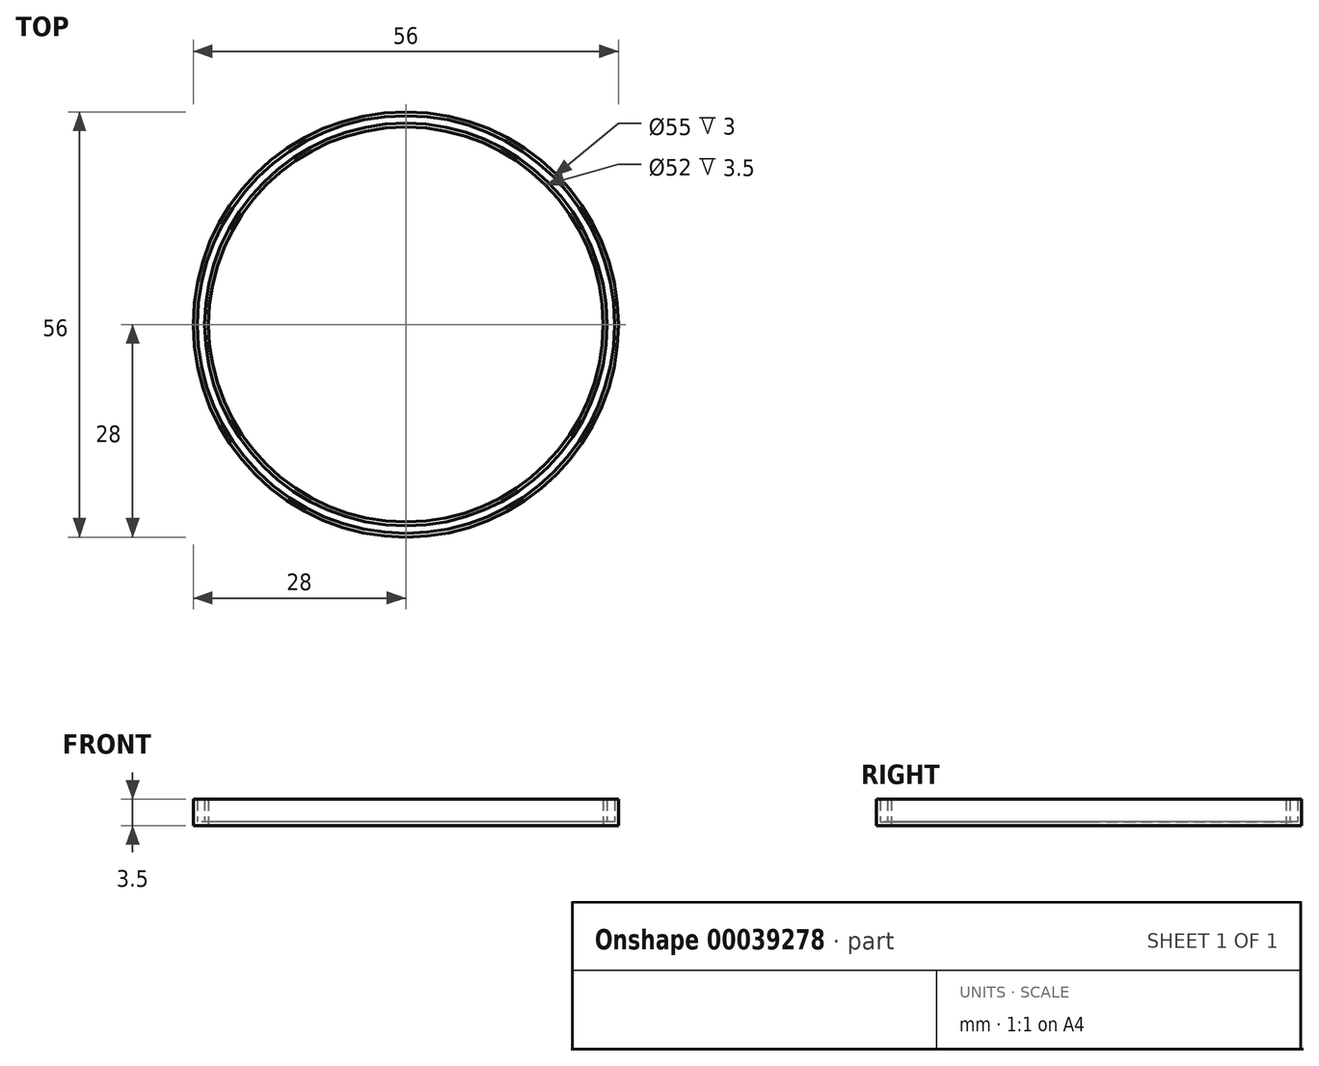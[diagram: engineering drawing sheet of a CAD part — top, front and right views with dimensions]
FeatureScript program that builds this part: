
annotation { "Feature Type Name" : "Feature", "Feature Type Description" : "" }
export const myFeature = defineFeature(function(context is Context, id is Id, definition is map)
    precondition{}
    {
        {
            var Q0;
            Q0=qCreatedBy(makeId("Top.planeOp"),FACE);
            var sketch = newSketch(context, id + "F0", { "sketchPlane" : qUnion([Q0])});
            skCircle(sketch, "E0", {"center": v(0, 0) * mm, "radius": 28 * mm});
            skCircle(sketch, "E1", {"center": v(0, 0) * mm, "radius": 27.5 * mm});
            skCircle(sketch, "E2.0", {"center": v(0, 0) * mm, "radius": 26.5 * mm});
            skCircle(sketch, "E3.0", {"center": v(0, 0) * mm, "radius": 26 * mm});
            skSolve(sketch);
        }
        {
            var Q0;
            Q0 = qSketchRegion(id + "F0", true);
            var Q1;
            Q1=makeQuery(id+"F0.imprint","IMPRINT",FACE,{"disambiguationData":[TD([[makeQuery(id+"F0.imprint","IMPRINT",EDGE,{"derivedFrom":sQuery(id+"F0.wireOp",EDGE,"E2.0")}),1.0]])]});
            extrude(context, id + "F1", {"entities" : qUnion([Q0, Q1]), "depth" : 3 * mm});
        }
        {
            var Q0;
            Q0=makeQuery(id+"F1.opExtrude","CAP_FACE",FACE,{"disambiguationData":[OSD([sQuery(id+"F0.wireOp",EDGE,"E0"),sQuery(id+"F0.wireOp",EDGE,"E1")])],"isStart":true});
            var sketch = newSketch(context, id + "F2", { "sketchPlane" : qUnion([Q0])});
            skCircle(sketch, "E4", {"center": v(0, 0) * mm, "radius": 28 * mm});
            skCircle(sketch, "E5", {"center": v(0, 0) * mm, "radius": 26 * mm});
            skSolve(sketch);
        }
        {
            var Q0;
            Q0 = qSketchRegion(id + "F2", true);
            extrude(context, id + "F3", {"entities" : qUnion([Q0]), "operationType" : NewBodyOperationType.ADD, "depth" : 0.5 * mm});
        }
    });
